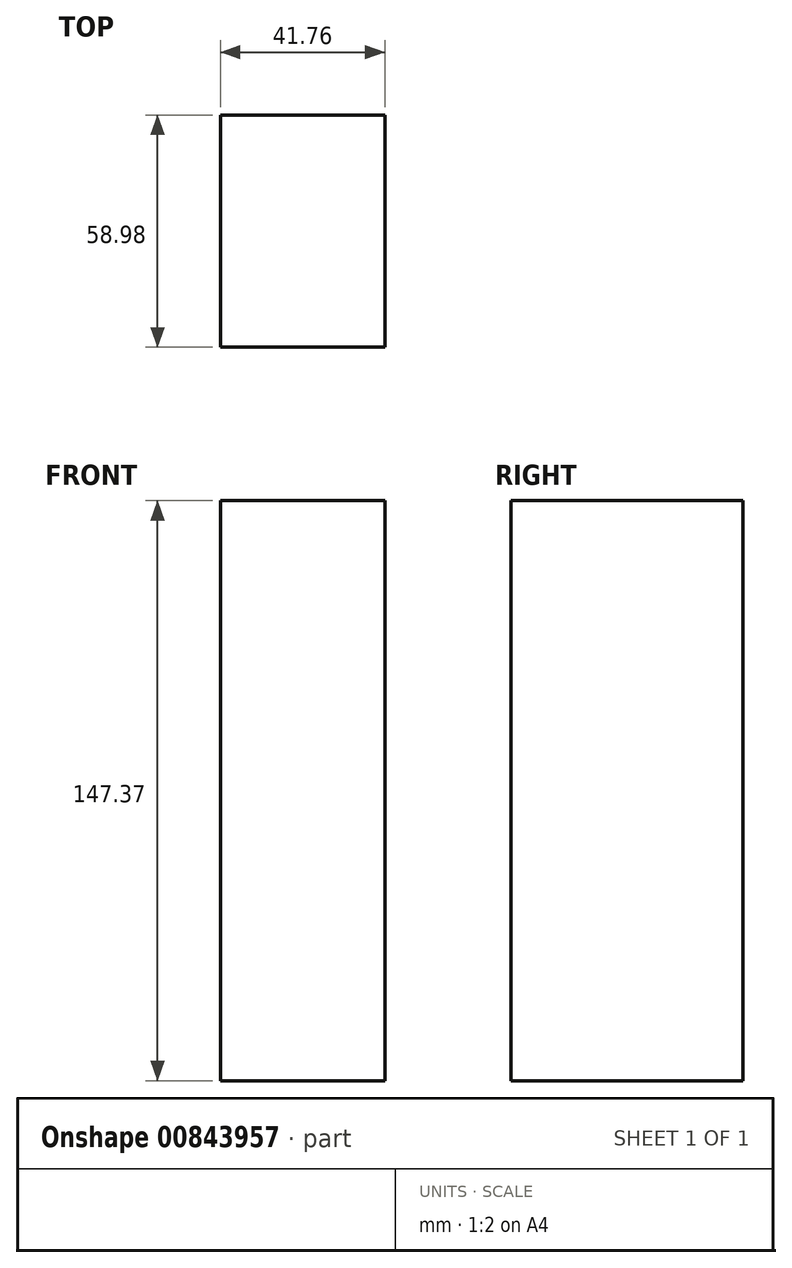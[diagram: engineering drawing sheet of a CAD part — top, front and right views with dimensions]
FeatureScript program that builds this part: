
annotation { "Feature Type Name" : "Feature", "Feature Type Description" : "" }
export const myFeature = defineFeature(function(context is Context, id is Id, definition is map)
    precondition{}
    {
        {
            var Q0;
            Q0=qCreatedBy(makeId("Front.planeOp"),FACE);
            var sketch = newSketch(context, id + "F0", { "sketchPlane" : qUnion([Q0])});
            skLineSegment(sketch, "E0.bottom", {"start": v(-41.76, 27.35) * mm, "end": v(0, 27.35) * mm});
            skLineSegment(sketch, "E0.top", {"start": v(-41.76, 49.15) * mm, "end": v(0, 49.15) * mm});
            skLineSegment(sketch, "E0.left", {"start": v(-41.76, 27.35) * mm, "end": v(-41.76, 49.15) * mm});
            skLineSegment(sketch, "E0.right", {"start": v(0, 27.35) * mm, "end": v(0, 49.15) * mm});
            skSolve(sketch);
        }
        {
            var Q0;
            Q0 = qSketchRegion(id + "F0", true);
            extrude(context, id + "F1", {"entities" : qUnion([Q0]), "depth" : 58.98 * mm, "offsetDistance" : 25.4 * mm});
        }
        {
            var Q0;
            Q0=makeQuery(id+"F1.opExtrude","SWEPT_FACE",FACE,{"disambiguationData":[OSD([sQuery(id+"F0.wireOp",EDGE,"E0.top")])]});
            shell(context, id + "F2", {"entities" : qUnion([Q0]), "thickness" : .1 * mm});
        }
        {
            var Q0;
            Q0=makeQuery(id+"F1.opExtrude","SWEPT_FACE",FACE,{"disambiguationData":[OSD([sQuery(id+"F0.wireOp",EDGE,"E0.bottom")])]});
            extrude(context, id + "F3", {"entities" : qUnion([Q0]), "operationType" : NewBodyOperationType.ADD, "oppositeDirection" : true, "depth" : 147.37 * mm, "offsetDistance" : 25.4 * mm});
        }
        {
            var Q0;
            Q0=makeQuery(id+"F3.opExtrude","CAP_FACE",FACE,{"disambiguationData":[OSD([sQuery(id+"F0.wireOp",EDGE,"E0.bottom")])],"isStart":false});
            extrude(context, id + "F4", {"entities" : qUnion([Q0]), "operationType" : NewBodyOperationType.ADD, "oppositeDirection" : true, "depth" : 21.1 * mm, "offsetDistance" : 25.4 * mm});
        }
    });
